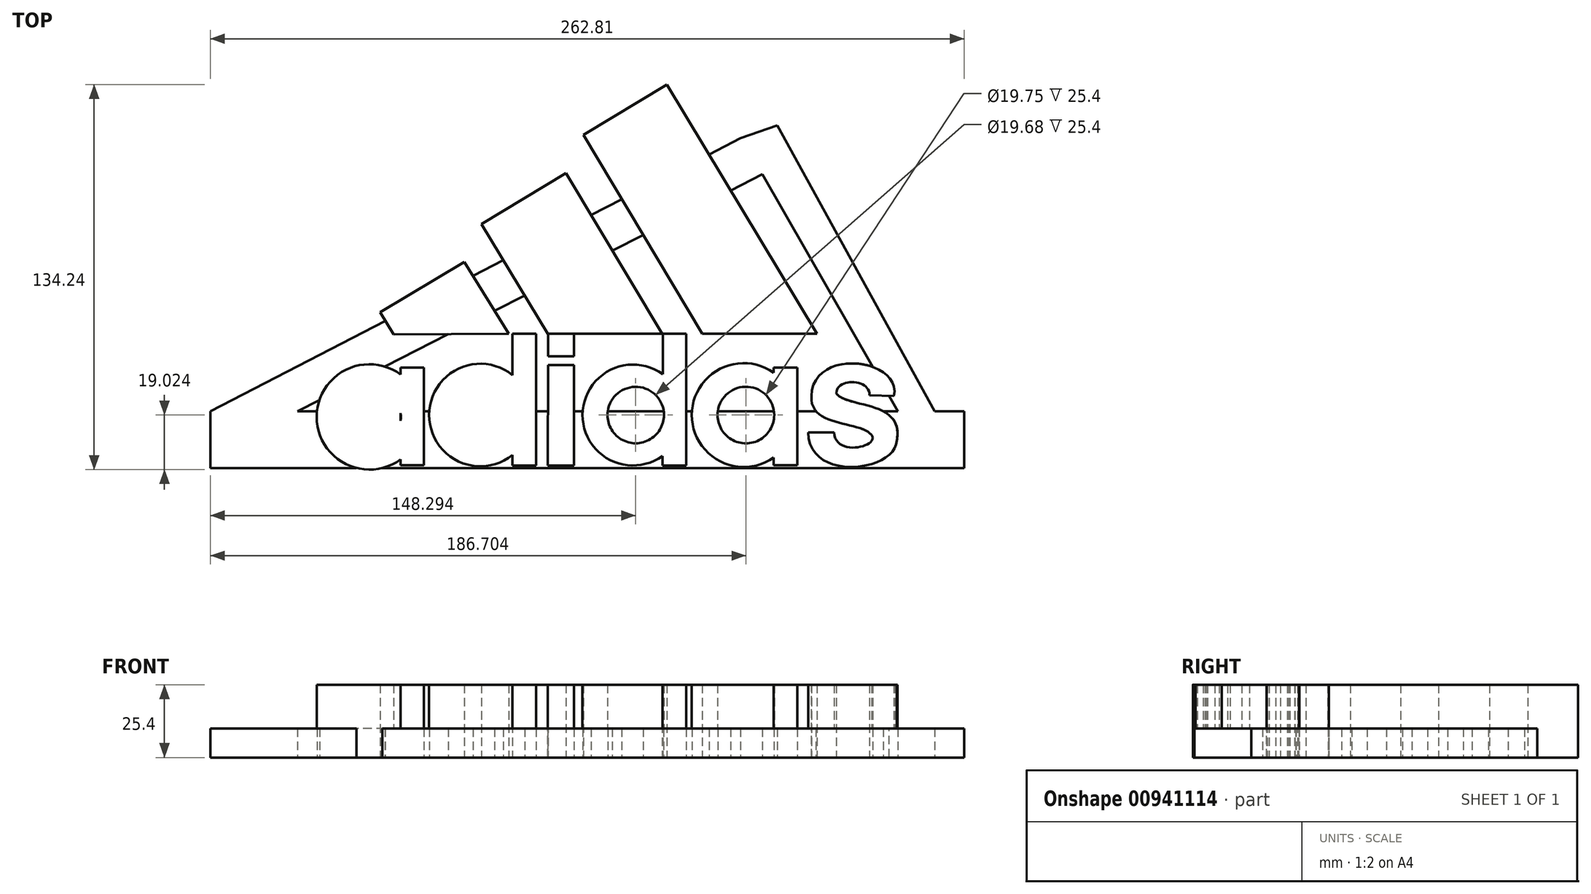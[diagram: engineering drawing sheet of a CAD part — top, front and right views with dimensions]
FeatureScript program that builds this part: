
annotation { "Feature Type Name" : "Feature", "Feature Type Description" : "" }
export const myFeature = defineFeature(function(context is Context, id is Id, definition is map)
    precondition{}
    {
        {
            var Q0;
            Q0=qCreatedBy(makeId("Top.planeOp"),FACE);
            var sketch = newSketch(context, id + "F0", { "sketchPlane" : qUnion([Q0])});
            skLineSegment(sketch, "E0", {"start": v(-70.9, -20.95) * mm, "end": v(-66.24, -28.76) * mm});
            skLineSegment(sketch, "E1", {"start": v(-70.9, -20.95) * mm, "end": v(-41.55, -3.47) * mm});
            skLineSegment(sketch, "E2", {"start": v(-41.55, -3.47) * mm, "end": v(-26.06, -28.5) * mm});
            skLineSegment(sketch, "E3", {"start": v(-26.06, -28.5) * mm, "end": v(-66.24, -28.76) * mm});
            skLineSegment(sketch, "E4", {"start": v(-35.53, 9.8) * mm, "end": v(-12.49, -28.39) * mm});
            skLineSegment(sketch, "E5", {"start": v(-12.49, -28.39) * mm, "end": v(27.37, -28.39) * mm});
            skLineSegment(sketch, "E6", {"start": v(27.37, -28.39) * mm, "end": v(-6.11, 27.53) * mm});
            skLineSegment(sketch, "E7", {"start": v(-6.11, 27.53) * mm, "end": v(-35.53, 9.8) * mm});
            skLineSegment(sketch, "E8", {"start": v(0, 40.86) * mm, "end": v(41.39, -28.47) * mm});
            skLineSegment(sketch, "E9", {"start": v(41.39, -28.47) * mm, "end": v(81.34, -28.47) * mm});
            skLineSegment(sketch, "E10", {"start": v(81.34, -28.47) * mm, "end": v(29.13, 58.4) * mm});
            skLineSegment(sketch, "E11", {"start": v(29.13, 58.4) * mm, "end": v(0, 40.86) * mm});
            skLineSegment(sketch, "E12", {"start": v(-91.66, -75.27) * mm, "end": v(132.72, -75.27) * mm});
            skLineSegment(sketch, "E13", {"start": v(132.72, -75.27) * mm, "end": v(132.72, -55.47) * mm});
            skLineSegment(sketch, "E14", {"start": v(132.72, -55.47) * mm, "end": v(-130.1, -55.47) * mm});
            skLineSegment(sketch, "E15", {"start": v(-130.1, -55.47) * mm, "end": v(-130.1, -75.27) * mm});
            skLineSegment(sketch, "E16", {"start": v(-130.1, -75.27) * mm, "end": v(-91.66, -75.27) * mm});
            skLineSegment(sketch, "E17", {"start": v(-130.1, -55.47) * mm, "end": v(54.77, 39.75) * mm});
            skLineSegment(sketch, "E18", {"start": v(54.77, 39.75) * mm, "end": v(62.39, 27.13) * mm});
            skLineSegment(sketch, "E19", {"start": v(62.39, 27.13) * mm, "end": v(-99.74, -55.47) * mm});
            skLineSegment(sketch, "E20", {"start": v(-99.74, -55.47) * mm, "end": v(62.39, 27.13) * mm});
            skLineSegment(sketch, "E21", {"start": v(109.62, -55.47) * mm, "end": v(62.39, 27.13) * mm});
            skLineSegment(sketch, "E22", {"start": v(54.77, 39.75) * mm, "end": v(67.54, 44.23) * mm});
            skLineSegment(sketch, "E23", {"start": v(67.54, 44.23) * mm, "end": v(122.38, -55.47) * mm});
            skSolve(sketch);
        }
        {
            var Q0;
            Q0=qCreatedBy(makeId("Top.planeOp"),FACE);
            var sketch = newSketch(context, id + "F1", { "sketchPlane" : qUnion([Q0])});
            skCircle(sketch, "E24", {"center": v(-73.49, -57.46) * mm, "radius": 9.82 * mm});
            skFitSpline(sketch, "E25", {"points": [v(108.23, -50.17) * mm, v(79.44, -50.22) * mm], "startDerivative": vector(7.66, 40.44) * mm, "endDerivative": vector(-0.61, -50.38) * mm});
            skFitSpline(sketch, "E26", {"points": [v(79.44, -50.22) * mm, v(100.4, -63.8) * mm], "startDerivative": vector(-2.1, -33.22) * mm, "endDerivative": vector(10.44, -14.89) * mm});
            skFitSpline(sketch, "E27", {"points": [v(100.4, -63.8) * mm, v(87.4, -62.9) * mm], "startDerivative": vector(9.17, -11.92) * mm, "endDerivative": vector(-0.76, 25.96) * mm});
            skFitSpline(sketch, "E28", {"points": [v(87.4, -62.9) * mm, v(78.33, -62.9) * mm], "startDerivative": vector(-9.07, 0) * mm, "endDerivative": vector(-9.07, 0) * mm});
            skFitSpline(sketch, "E29", {"points": [v(78.33, -62.9) * mm, v(109.2, -65.73) * mm], "startDerivative": vector(0.67, -52.23) * mm, "endDerivative": vector(1.08, 32.5) * mm});
            skFitSpline(sketch, "E30", {"points": [v(109.2, -65.73) * mm, v(88.14, -49.26) * mm], "startDerivative": vector(8.16, 42.94) * mm, "endDerivative": vector(-10.97, 15.63) * mm});
            skFitSpline(sketch, "E31", {"points": [v(88.14, -49.26) * mm, v(99.7, -49.9) * mm], "startDerivative": vector(0.01, 16.48) * mm, "endDerivative": vector(-0.57, -17.53) * mm});
            skFitSpline(sketch, "E32", {"points": [v(99.7, -49.9) * mm, v(108.23, -50.17) * mm], "startDerivative": vector(8.53, -0.27) * mm, "endDerivative": vector(8.53, -0.27) * mm});
            skCircle(sketch, "E33", {"center": v(-34.58, -56.8) * mm, "radius": 10.05 * mm});
            skCircle(sketch, "E34", {"center": v(18.2, -56.8) * mm, "radius": 9.84 * mm});
            skCircle(sketch, "E35", {"center": v(56.61, -56.8) * mm, "radius": 9.87 * mm});
            skCircle(sketch, "E36", {"center": v(-35.94, -56.8) * mm, "radius": 17.88 * mm});
            skCircle(sketch, "E37", {"center": v(17.26, -56.8) * mm, "radius": 17.6 * mm});
            skCircle(sketch, "E38", {"center": v(-74.64, -57.46) * mm, "radius": 18.37 * mm});
            skCircle(sketch, "E39", {"center": v(55.86, -56.8) * mm, "radius": 18.11 * mm});
            skLineSegment(sketch, "E40", {"start": v(-63.76, -40.26) * mm, "end": v(-55.68, -40.26) * mm});
            skLineSegment(sketch, "E41", {"start": v(-55.68, -40.26) * mm, "end": v(-55.68, -74.3) * mm});
            skLineSegment(sketch, "E42", {"start": v(-55.68, -74.3) * mm, "end": v(-63.75, -74.3) * mm});
            skLineSegment(sketch, "E43", {"start": v(-63.75, -74.3) * mm, "end": v(-63.76, -40.26) * mm});
            skLineSegment(sketch, "E44", {"start": v(-24.72, -28.46) * mm, "end": v(-16.5, -28.46) * mm});
            skLineSegment(sketch, "E45", {"start": v(-16.5, -28.46) * mm, "end": v(-16.5, -74.41) * mm});
            skLineSegment(sketch, "E46", {"start": v(-16.5, -74.41) * mm, "end": v(-24.77, -74.42) * mm});
            skLineSegment(sketch, "E47", {"start": v(-24.77, -74.42) * mm, "end": v(-24.72, -28.46) * mm});
            skLineSegment(sketch, "E48", {"start": v(-12.4, -39.36) * mm, "end": v(-3.34, -39.4) * mm});
            skLineSegment(sketch, "E49", {"start": v(-3.34, -39.4) * mm, "end": v(-3.34, -74.42) * mm});
            skLineSegment(sketch, "E50", {"start": v(-3.34, -74.42) * mm, "end": v(-12.45, -74.42) * mm});
            skLineSegment(sketch, "E51", {"start": v(-12.45, -74.42) * mm, "end": v(-12.4, -39.36) * mm});
            skLineSegment(sketch, "E52", {"start": v(27.67, -28.46) * mm, "end": v(35.76, -28.46) * mm});
            skLineSegment(sketch, "E53", {"start": v(35.76, -28.46) * mm, "end": v(35.76, -74.42) * mm});
            skLineSegment(sketch, "E54", {"start": v(35.76, -74.42) * mm, "end": v(27.52, -74.41) * mm});
            skLineSegment(sketch, "E55", {"start": v(27.52, -74.41) * mm, "end": v(27.67, -28.46) * mm});
            skLineSegment(sketch, "E56", {"start": v(66.33, -40.26) * mm, "end": v(74.58, -40.32) * mm});
            skLineSegment(sketch, "E57", {"start": v(74.58, -40.32) * mm, "end": v(74.58, -74.3) * mm});
            skLineSegment(sketch, "E58", {"start": v(74.58, -74.3) * mm, "end": v(66.32, -74.3) * mm});
            skLineSegment(sketch, "E59", {"start": v(66.32, -74.3) * mm, "end": v(66.33, -40.26) * mm});
            skLineSegment(sketch, "E60", {"start": v(-12.4, -28.46) * mm, "end": v(-3.34, -28.47) * mm});
            skLineSegment(sketch, "E61", {"start": v(-3.34, -28.47) * mm, "end": v(-3.34, -36.39) * mm});
            skLineSegment(sketch, "E62", {"start": v(-3.34, -36.39) * mm, "end": v(-12.4, -36.39) * mm});
            skLineSegment(sketch, "E63", {"start": v(-12.4, -36.39) * mm, "end": v(-12.4, -28.46) * mm});
            skSolve(sketch);
        }
        {
            var Q0;
            {var subQ0=sQuery(id+"F1.wireOp",EDGE,"E43");var subQ1=sQuery(id+"F1.wireOp",EDGE,"E24");var subQ2=makeQuery(id+"F1.imprint","INTERSECT",VERTEX,{"disambiguationData":[OD(0.0)],"derivedFrom":[subQ1,subQ0]});Q0=makeQuery(id+"F1.imprint","IMPRINT",FACE,{"disambiguationData":[TD([[makeQuery(id+"F1.imprint","IMPRINT",EDGE,{"disambiguationData":[TD([[subQ2,1.0]])],"derivedFrom":subQ1}),-1.0]])]});}
            var Q1;
            {var subQ0=sQuery(id+"F1.wireOp",EDGE,"E47");var subQ1=sQuery(id+"F1.wireOp",EDGE,"E33");var subQ2=makeQuery(id+"F1.imprint","INTERSECT",VERTEX,{"disambiguationData":[OD(0.0)],"derivedFrom":[subQ1,subQ0]});Q1=makeQuery(id+"F1.imprint","IMPRINT",FACE,{"disambiguationData":[TD([[makeQuery(id+"F1.imprint","IMPRINT",EDGE,{"disambiguationData":[TD([[subQ2,1.0]])],"derivedFrom":subQ1}),-1.0]])]});}
            var Q2;
            {var subQ0=sQuery(id+"F1.wireOp",EDGE,"E40");Q2=makeQuery(id+"F1.imprint","IMPRINT",FACE,{"disambiguationData":[TD([[makeQuery(id+"F1.imprint","IMPRINT",EDGE,{"derivedFrom":subQ0}),-1.0]])]});}
            var Q3;
            {var subQ1=sQuery(id+"F1.wireOp",EDGE,"E44");Q3=makeQuery(id+"F1.imprint","IMPRINT",FACE,{"disambiguationData":[TD([[makeQuery(id+"F1.imprint","IMPRINT",EDGE,{"derivedFrom":subQ1}),-1.0]])]});}
            var Q4;
            Q4=makeQuery(id+"F1.imprint","IMPRINT",FACE,{"disambiguationData":[TD([[makeQuery(id+"F1.imprint","IMPRINT",EDGE,{"derivedFrom":sQuery(id+"F1.wireOp",EDGE,"E60")}),-1.0]])]});
            var Q5;
            {var subQ0=sQuery(id+"F1.wireOp",EDGE,"E55");var subQ1=sQuery(id+"F1.wireOp",EDGE,"E34");var subQ2=makeQuery(id+"F1.imprint","INTERSECT",VERTEX,{"disambiguationData":[OD(0.0)],"derivedFrom":[subQ1,subQ0]});Q5=makeQuery(id+"F1.imprint","IMPRINT",FACE,{"disambiguationData":[TD([[makeQuery(id+"F1.imprint","IMPRINT",EDGE,{"disambiguationData":[TD([[subQ2,1.0]])],"derivedFrom":subQ1}),-1.0]])]});}
            var Q6;
            Q6=makeQuery(id+"F1.imprint","IMPRINT",FACE,{"disambiguationData":[TD([[makeQuery(id+"F1.imprint","IMPRINT",EDGE,{"derivedFrom":sQuery(id+"F1.wireOp",EDGE,"E48")}),-1.0]])]});
            var Q7;
            {var subQ0=sQuery(id+"F1.wireOp",EDGE,"E55");var subQ1=sQuery(id+"F1.wireOp",EDGE,"E34");var subQ2=makeQuery(id+"F1.imprint","INTERSECT",VERTEX,{"disambiguationData":[OD(0.0)],"derivedFrom":[subQ1,subQ0]});Q7=makeQuery(id+"F1.imprint","IMPRINT",FACE,{"disambiguationData":[TD([[makeQuery(id+"F1.imprint","IMPRINT",EDGE,{"disambiguationData":[TD([[subQ2,-1.0]])],"derivedFrom":subQ1}),-1.0]])]});}
            var Q8;
            {var subQ1=sQuery(id+"F1.wireOp",EDGE,"E52");Q8=makeQuery(id+"F1.imprint","IMPRINT",FACE,{"disambiguationData":[TD([[makeQuery(id+"F1.imprint","IMPRINT",EDGE,{"derivedFrom":subQ1}),-1.0]])]});}
            var Q9;
            {var subQ0=sQuery(id+"F1.wireOp",EDGE,"E59");var subQ1=sQuery(id+"F1.wireOp",EDGE,"E35");var subQ2=makeQuery(id+"F1.imprint","INTERSECT",VERTEX,{"disambiguationData":[OD(0.0)],"derivedFrom":[subQ1,subQ0]});Q9=makeQuery(id+"F1.imprint","IMPRINT",FACE,{"disambiguationData":[TD([[makeQuery(id+"F1.imprint","IMPRINT",EDGE,{"disambiguationData":[TD([[subQ2,1.0]])],"derivedFrom":subQ1}),-1.0]])]});}
            var Q10;
            {var subQ0=sQuery(id+"F1.wireOp",EDGE,"E59");var subQ1=sQuery(id+"F1.wireOp",EDGE,"E35");var subQ2=makeQuery(id+"F1.imprint","INTERSECT",VERTEX,{"disambiguationData":[OD(0.0)],"derivedFrom":[subQ1,subQ0]});Q10=makeQuery(id+"F1.imprint","IMPRINT",FACE,{"disambiguationData":[TD([[makeQuery(id+"F1.imprint","IMPRINT",EDGE,{"disambiguationData":[TD([[subQ2,-1.0]])],"derivedFrom":subQ1}),-1.0]])]});}
            var Q11;
            Q11=makeQuery(id+"F1.imprint","IMPRINT",FACE,{"disambiguationData":[TD([[makeQuery(id+"F1.imprint","IMPRINT",EDGE,{"derivedFrom":sQuery(id+"F1.wireOp",EDGE,"E25")}),1.0]])]});
            var Q12;
            Q12=makeQuery(id+"F0.imprint","IMPRINT",FACE,{"disambiguationData":[TD([[makeQuery(id+"F0.imprint","IMPRINT",EDGE,{"derivedFrom":sQuery(id+"F0.wireOp",EDGE,"E8")}),1.0]])]});
            var Q13;
            Q13=makeQuery(id+"F0.imprint","IMPRINT",FACE,{"disambiguationData":[TD([[makeQuery(id+"F0.imprint","IMPRINT",EDGE,{"derivedFrom":sQuery(id+"F0.wireOp",EDGE,"E4")}),1.0]])]});
            var Q14;
            Q14=makeQuery(id+"F0.imprint","IMPRINT",FACE,{"disambiguationData":[TD([[makeQuery(id+"F0.imprint","IMPRINT",EDGE,{"derivedFrom":sQuery(id+"F0.wireOp",EDGE,"E0")}),1.0]])]});
            var Q15;
            {var subQ1=sQuery(id+"F1.wireOp",EDGE,"E56");Q15=makeQuery(id+"F1.imprint","IMPRINT",FACE,{"disambiguationData":[TD([[makeQuery(id+"F1.imprint","IMPRINT",EDGE,{"derivedFrom":subQ1}),-1.0]])]});}
            var Q16;
            {var subQ0=sQuery(id+"F1.wireOp",EDGE,"E43");var subQ1=sQuery(id+"F1.wireOp",EDGE,"E24");var subQ2=makeQuery(id+"F1.imprint","INTERSECT",VERTEX,{"disambiguationData":[OD(0.0)],"derivedFrom":[subQ1,subQ0]});Q16=makeQuery(id+"F1.imprint","IMPRINT",FACE,{"disambiguationData":[TD([[makeQuery(id+"F1.imprint","IMPRINT",EDGE,{"disambiguationData":[TD([[subQ2,-1.0]])],"derivedFrom":subQ1}),1.0]])]});}
            var Q17;
            {var subQ0=sQuery(id+"F1.wireOp",EDGE,"xkdoKZ9v-5MWE-QOwO-j5dc-XWh7lJoWMzYW");var subQ1=sQuery(id+"F1.wireOp",EDGE,"E24");var subQ2=makeQuery(id+"F1.imprint","INTERSECT",VERTEX,{"derivedFrom":[subQ1,subQ0]});Q17=makeQuery(id+"F1.imprint","IMPRINT",FACE,{"disambiguationData":[TD([[makeQuery(id+"F1.imprint","IMPRINT",EDGE,{"disambiguationData":[TD([[subQ2,1.0]])],"derivedFrom":subQ1}),-1.0]])]});}
            var Q18;
            {var subQ0=sQuery(id+"F1.wireOp",EDGE,"E43");var subQ1=sQuery(id+"F1.wireOp",EDGE,"E24");var subQ2=makeQuery(id+"F1.imprint","INTERSECT",VERTEX,{"disambiguationData":[OD(0.0)],"derivedFrom":[subQ1,subQ0]});Q18=makeQuery(id+"F1.imprint","IMPRINT",FACE,{"disambiguationData":[TD([[makeQuery(id+"F1.imprint","IMPRINT",EDGE,{"disambiguationData":[TD([[subQ2,-1.0]])],"derivedFrom":subQ1}),-1.0]])]});}
            var Q19;
            {var subQ1=sQuery(id+"F1.wireOp",EDGE,"E42");Q19=makeQuery(id+"F1.imprint","IMPRINT",FACE,{"disambiguationData":[TD([[makeQuery(id+"F1.imprint","IMPRINT",EDGE,{"derivedFrom":subQ1}),-1.0]])]});}
            var Q20;
            {var subQ0=sQuery(id+"F1.wireOp",EDGE,"xkdoKZ9v-5MWE-QOwO-j5dc-XWh7lJoWMzYW");var subQ1=sQuery(id+"F1.wireOp",EDGE,"E33");var subQ2=makeQuery(id+"F1.imprint","INTERSECT",VERTEX,{"disambiguationData":[OD(0.0)],"derivedFrom":[subQ1,subQ0]});Q20=makeQuery(id+"F1.imprint","IMPRINT",FACE,{"disambiguationData":[TD([[makeQuery(id+"F1.imprint","IMPRINT",EDGE,{"disambiguationData":[TD([[subQ2,-1.0]])],"derivedFrom":subQ1}),1.0]])]});}
            var Q21;
            {var subQ0=sQuery(id+"F1.wireOp",EDGE,"xkdoKZ9v-5MWE-QOwO-j5dc-XWh7lJoWMzYW");var subQ1=sQuery(id+"F1.wireOp",EDGE,"E33");var subQ2=makeQuery(id+"F1.imprint","INTERSECT",VERTEX,{"disambiguationData":[OD(0.0)],"derivedFrom":[subQ1,subQ0]});Q21=makeQuery(id+"F1.imprint","IMPRINT",FACE,{"disambiguationData":[TD([[makeQuery(id+"F1.imprint","IMPRINT",EDGE,{"disambiguationData":[TD([[subQ2,1.0]])],"derivedFrom":subQ1}),1.0]])]});}
            var Q22;
            {var subQ0=sQuery(id+"F1.wireOp",EDGE,"xkdoKZ9v-5MWE-QOwO-j5dc-XWh7lJoWMzYW");var subQ1=sQuery(id+"F1.wireOp",EDGE,"E33");var subQ2=makeQuery(id+"F1.imprint","INTERSECT",VERTEX,{"disambiguationData":[OD(0.0)],"derivedFrom":[subQ1,subQ0]});Q22=makeQuery(id+"F1.imprint","IMPRINT",FACE,{"disambiguationData":[TD([[makeQuery(id+"F1.imprint","IMPRINT",EDGE,{"disambiguationData":[TD([[subQ2,1.0]])],"derivedFrom":subQ1}),-1.0]])]});}
            var Q23;
            {var subQ0=sQuery(id+"F1.wireOp",EDGE,"xkdoKZ9v-5MWE-QOwO-j5dc-XWh7lJoWMzYW");var subQ1=sQuery(id+"F1.wireOp",EDGE,"E33");var subQ2=makeQuery(id+"F1.imprint","INTERSECT",VERTEX,{"disambiguationData":[OD(0.0)],"derivedFrom":[subQ1,subQ0]});Q23=makeQuery(id+"F1.imprint","IMPRINT",FACE,{"disambiguationData":[TD([[makeQuery(id+"F1.imprint","IMPRINT",EDGE,{"disambiguationData":[TD([[subQ2,-1.0]])],"derivedFrom":subQ1}),-1.0]])]});}
            var Q24;
            {var subQ1=sQuery(id+"F1.wireOp",EDGE,"E46");Q24=makeQuery(id+"F1.imprint","IMPRINT",FACE,{"disambiguationData":[TD([[makeQuery(id+"F1.imprint","IMPRINT",EDGE,{"derivedFrom":subQ1}),-1.0]])]});}
            var Q25;
            {var subQ0=sQuery(id+"F1.wireOp",EDGE,"E50");Q25=makeQuery(id+"F1.imprint","IMPRINT",FACE,{"disambiguationData":[TD([[makeQuery(id+"F1.imprint","IMPRINT",EDGE,{"derivedFrom":subQ0}),-1.0]])]});}
            var Q26;
            {var subQ0=sQuery(id+"F1.wireOp",EDGE,"xkdoKZ9v-5MWE-QOwO-j5dc-XWh7lJoWMzYW");var subQ1=sQuery(id+"F1.wireOp",EDGE,"E34");var subQ2=makeQuery(id+"F1.imprint","INTERSECT",VERTEX,{"disambiguationData":[OD(0.0)],"derivedFrom":[subQ1,subQ0]});Q26=makeQuery(id+"F1.imprint","IMPRINT",FACE,{"disambiguationData":[TD([[makeQuery(id+"F1.imprint","IMPRINT",EDGE,{"disambiguationData":[TD([[subQ2,-1.0]])],"derivedFrom":subQ1}),-1.0]])]});}
            var Q27;
            {var subQ1=sQuery(id+"F1.wireOp",EDGE,"E54");Q27=makeQuery(id+"F1.imprint","IMPRINT",FACE,{"disambiguationData":[TD([[makeQuery(id+"F1.imprint","IMPRINT",EDGE,{"derivedFrom":subQ1}),-1.0]])]});}
            var Q28;
            {var subQ0=sQuery(id+"F1.wireOp",EDGE,"xkdoKZ9v-5MWE-QOwO-j5dc-XWh7lJoWMzYW");var subQ1=sQuery(id+"F1.wireOp",EDGE,"E35");var subQ2=makeQuery(id+"F1.imprint","INTERSECT",VERTEX,{"disambiguationData":[OD(0.0)],"derivedFrom":[subQ1,subQ0]});Q28=makeQuery(id+"F1.imprint","IMPRINT",FACE,{"disambiguationData":[TD([[makeQuery(id+"F1.imprint","IMPRINT",EDGE,{"disambiguationData":[TD([[subQ2,-1.0]])],"derivedFrom":subQ1}),-1.0]])]});}
            var Q29;
            {var subQ1=sQuery(id+"F1.wireOp",EDGE,"E58");Q29=makeQuery(id+"F1.imprint","IMPRINT",FACE,{"disambiguationData":[TD([[makeQuery(id+"F1.imprint","IMPRINT",EDGE,{"derivedFrom":subQ1}),-1.0]])]});}
            var Q30;
            {var subQ1=sQuery(id+"F1.wireOp",EDGE,"E27");Q30=makeQuery(id+"F1.imprint","IMPRINT",FACE,{"disambiguationData":[TD([[makeQuery(id+"F1.imprint","IMPRINT",EDGE,{"derivedFrom":subQ1}),1.0]])]});}
            var Q31;
            {var subQ1=sQuery(id+"F0.wireOp",EDGE,"E0");var subQ5=sQuery(id+"F0.wireOp",EDGE,"E3");var subQ6=makeQuery(id+"F0.imprint","INTERSECT",VERTEX,{"derivedFrom":[subQ1,subQ5]});Q31=makeQuery(id+"F0.imprint","IMPRINT",FACE,{"disambiguationData":[TD([[makeQuery(id+"F0.imprint","IMPRINT",EDGE,{"disambiguationData":[TD([[subQ6,1.0]])],"derivedFrom":subQ1}),1.0]])]});}
            var Q32;
            {var subQ0=sQuery(id+"F0.wireOp",EDGE,"E3");var subQ1=sQuery(id+"F0.wireOp",EDGE,"E2");var subQ2=makeQuery(id+"F0.imprint","INTERSECT",VERTEX,{"derivedFrom":[subQ1,subQ0]});Q32=makeQuery(id+"F0.imprint","IMPRINT",FACE,{"disambiguationData":[TD([[makeQuery(id+"F0.imprint","IMPRINT",EDGE,{"disambiguationData":[TD([[subQ2,1.0]])],"derivedFrom":subQ1}),-1.0]])]});}
            var Q33;
            {var subQ0=sQuery(id+"F0.wireOp",EDGE,"YEG5WHaX-31RR-nVnb-hpmy-JsCladpTtrkE");Q33=makeQuery(id+"F0.imprint","IMPRINT",FACE,{"disambiguationData":[TD([[makeQuery(id+"F0.imprint","IMPRINT",EDGE,{"derivedFrom":subQ0}),-1.0]])]});}
            var Q34;
            {var subQ5=sQuery(id+"F0.wireOp",EDGE,"nAT3AgK5-jm91-jzoL-Jk1j-64SNk6I07CwW");Q34=makeQuery(id+"F0.imprint","IMPRINT",FACE,{"disambiguationData":[TD([[makeQuery(id+"F0.imprint","IMPRINT",EDGE,{"derivedFrom":subQ5}),-1.0]])]});}
            extrude(context, id + "F2", {"entities" : qUnion([Q0, Q1, Q2, Q3, Q4, Q5, Q6, Q7, Q8, Q9, Q10, Q11, Q12, Q13, Q14, Q15, Q16, Q17, Q18, Q19, Q20, Q21, Q22, Q23, Q24, Q25, Q26, Q27, Q28, Q29, Q30, Q31, Q32, Q33, Q34]), "depth" : 25.4 * mm, "offsetDistance" : 25.4 * mm});
        }
        {
            var Q0;
            Q0=makeQuery(id+"F0.imprint","IMPRINT",FACE,{"disambiguationData":[TD([[makeQuery(id+"F0.imprint","IMPRINT",EDGE,{"derivedFrom":sQuery(id+"F0.wireOp",EDGE,"E18")}),1.0]])]});
            var Q1;
            {var subQ5=sQuery(id+"F0.wireOp",EDGE,"E18");Q1=makeQuery(id+"F0.imprint","IMPRINT",FACE,{"disambiguationData":[TD([[makeQuery(id+"F0.imprint","IMPRINT",EDGE,{"derivedFrom":subQ5}),-1.0]])]});}
            var Q2;
            {var subQ5=sQuery(id+"F0.wireOp",EDGE,"E3");var subQ6=sQuery(id+"F0.wireOp",EDGE,"E0");var subQ7=makeQuery(id+"F0.imprint","INTERSECT",VERTEX,{"derivedFrom":[subQ6,subQ5]});Q2=makeQuery(id+"F0.imprint","IMPRINT",FACE,{"disambiguationData":[TD([[makeQuery(id+"F0.imprint","IMPRINT",EDGE,{"disambiguationData":[TD([[subQ7,1.0]])],"derivedFrom":subQ6}),-1.0]])]});}
            var Q3;
            {var subQ0=sQuery(id+"F0.wireOp",EDGE,"E17");var subQ1=sQuery(id+"F0.wireOp",EDGE,"E2");var subQ2=makeQuery(id+"F0.imprint","INTERSECT",VERTEX,{"derivedFrom":[subQ1,subQ0]});Q3=makeQuery(id+"F0.imprint","IMPRINT",FACE,{"disambiguationData":[TD([[makeQuery(id+"F0.imprint","IMPRINT",EDGE,{"disambiguationData":[TD([[subQ2,-1.0]])],"derivedFrom":subQ1}),1.0]])]});}
            var Q4;
            {var subQ0=sQuery(id+"F0.wireOp",EDGE,"E17");var subQ1=sQuery(id+"F0.wireOp",EDGE,"E6");var subQ2=makeQuery(id+"F0.imprint","INTERSECT",VERTEX,{"derivedFrom":[subQ1,subQ0]});Q4=makeQuery(id+"F0.imprint","IMPRINT",FACE,{"disambiguationData":[TD([[makeQuery(id+"F0.imprint","IMPRINT",EDGE,{"disambiguationData":[TD([[subQ2,1.0]])],"derivedFrom":subQ1}),-1.0]])]});}
            var Q5;
            Q5=makeQuery(id+"F0.imprint","IMPRINT",FACE,{"disambiguationData":[TD([[makeQuery(id+"F0.imprint","IMPRINT",EDGE,{"derivedFrom":sQuery(id+"F0.wireOp",EDGE,"E12")}),1.0]])]});
            extrude(context, id + "F3", {"entities" : qUnion([Q0, Q1, Q2, Q3, Q4, Q5]), "operationType" : NewBodyOperationType.ADD, "depth" : 10.16 * mm, "offsetDistance" : 25.4 * mm});
        }
    });
